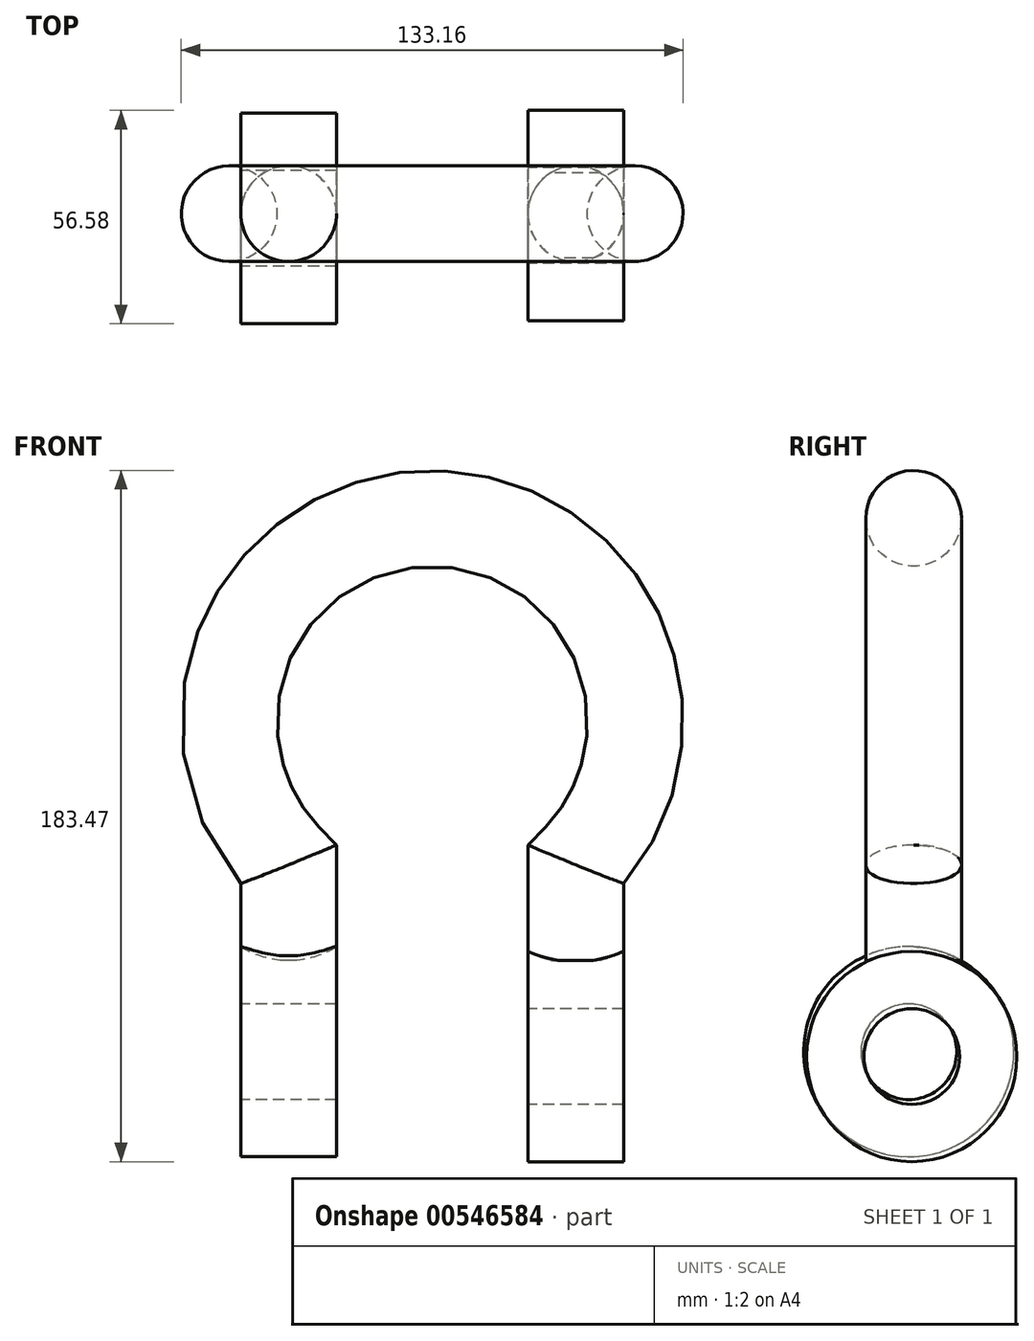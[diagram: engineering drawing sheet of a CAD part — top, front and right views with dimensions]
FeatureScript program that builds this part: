
annotation { "Feature Type Name" : "Feature", "Feature Type Description" : "" }
export const myFeature = defineFeature(function(context is Context, id is Id, definition is map)
    precondition{}
    {
        {
            var Q0;
            Q0=qCreatedBy(makeId("Top.planeOp"),FACE);
            var sketch = newSketch(context, id + "F0", { "sketchPlane" : qUnion([Q0])});
            skCircle(sketch, "E0", {"center": v(0, 0) * mm, "radius": 12.7 * mm});
            skSolve(sketch);
        }
        {
            var Q0;
            Q0=qCreatedBy(makeId("Front.planeOp"),FACE);
            var sketch = newSketch(context, id + "F1", { "sketchPlane" : qUnion([Q0])});
            skLineSegment(sketch, "E1", {"start": v(0, 0) * mm, "end": v(0, 25.4) * mm});
            skLineSegment(sketch, "E2", {"start": v(76.2, 0) * mm, "end": v(76.2, 25.4) * mm});
            skArc(sketch, "E3", {"start": v(76.2, 25.4) * mm, "mid": v(38.1, 117.38) * mm, "end": v(0, 25.4) * mm});
            skSolve(sketch);
        }
        {
            var Q0;
            Q0=makeQuery(id+"F0.imprint","IMPRINT",FACE,{"disambiguationData":[TD([[makeQuery(id+"F0.imprint","IMPRINT",EDGE,{"derivedFrom":sQuery(id+"F0.wireOp",EDGE,"E0")}),1.0]])]});
            var Q1;
            Q1=sQuery(id+"F1.wireOp",EDGE,"E3");
            var Q2;
            Q2=sQuery(id+"F1.wireOp",EDGE,"E1");
            var Q3;
            Q3=sQuery(id+"F1.wireOp",EDGE,"E2");
            sweep(context, id + "F2", {"profiles" : qUnion([Q0]), "path" : qUnion([Q1, Q2, Q3])});
        }
        {
            var Q0;
            Q0=qCreatedBy(makeId("Right.planeOp"),FACE);
            var sketch = newSketch(context, id + "F3", { "sketchPlane" : qUnion([Q0])});
            skLineSegment(sketch, "E4", {"start": v(12.7, 25.4) * mm, "end": v(12.7, 0) * mm});
            skLineSegment(sketch, "E5", {"start": v(-12.7, 1.3) * mm, "end": v(-12.7, 25.4) * mm});
            skArc(sketch, "E6", {"start": v(-12.7, 1.3) * mm, "mid": v(-2.7, -52.1) * mm, "end": v(12.7, 0) * mm});
            skCircle(sketch, "E7", {"center": v(-1.27, -24.2) * mm, "radius": 12.7 * mm});
            skLineSegment(sketch, "E8", {"start": v(0, 0) * mm, "end": v(-1.27, -24.2) * mm, "construction": true});
            skCircle(sketch, "E9", {"center": v(-1.27, -24.2) * mm, "radius": 27.9 * mm});
            skSolve(sketch);
        }
        {
            var Q0;
            Q0=makeQuery(id+"F3.imprint","IMPRINT",FACE,{"disambiguationData":[TD([[makeQuery(id+"F3.imprint","IMPRINT",EDGE,{"derivedFrom":sQuery(id+"F3.wireOp",EDGE,"E7")}),-1.0]])]});
            var Q1;
            Q1=makeQuery(id+"F2.opSweep","CAP_FACE",FACE,{"disambiguationData":[OSD([sQuery(id+"F0.wireOp",EDGE,"E0"),sQuery(id+"F1.wireOp",VERTEX,"E2.start")])],"isStart":false});
            extrude(context, id + "F4", {"entities" : qUnion([Q0]), "operationType" : NewBodyOperationType.ADD, "depth" : 12.7 * mm, "endBoundEntityFace" : qUnion([Q1]), "offsetDistance" : 25.4 * mm, "hasSecondDirection" : true, "secondDirectionOppositeDirection" : true, "secondDirectionDepth" : 12.7 * mm});
        }
        {
            var Q0;
            Q0=qCreatedBy(makeId("Right.planeOp"),FACE);
            cPlane(context, id + "F5", {"entities" : qUnion([Q0]), "cplaneType" : CPlaneType.OFFSET, "offset" : 76.2 * mm, "width" : 152.4 * mm, "height" : 152.4 * mm});
        }
        {
            var Q0;
            Q0=qCreatedBy(id+"F5.planeOp",FACE);
            var sketch = newSketch(context, id + "F6", { "sketchPlane" : qUnion([Q0])});
            skLineSegment(sketch, "E10", {"start": v(13.48, 24.1) * mm, "end": v(13.48, -1.3) * mm});
            skLineSegment(sketch, "E11", {"start": v(-11.92, 0) * mm, "end": v(-11.92, 24.1) * mm});
            skArc(sketch, "E12", {"start": v(-11.92, 0) * mm, "mid": v(-1.91, -53.4) * mm, "end": v(13.48, -1.3) * mm});
            skCircle(sketch, "E13", {"center": v(-0.49, -25.5) * mm, "radius": 12.7 * mm});
            skLineSegment(sketch, "E14", {"start": v(0.78, -1.3) * mm, "end": v(-0.49, -25.5) * mm, "construction": true});
            skCircle(sketch, "E15", {"center": v(-0.49, -25.5) * mm, "radius": 27.9 * mm});
            skSolve(sketch);
        }
        {
            var Q0;
            Q0=makeQuery(id+"F6.imprint","IMPRINT",FACE,{"disambiguationData":[TD([[makeQuery(id+"F6.imprint","IMPRINT",EDGE,{"derivedFrom":sQuery(id+"F6.wireOp",EDGE,"E13")}),-1.0]])]});
            extrude(context, id + "F7", {"entities" : qUnion([Q0]), "operationType" : NewBodyOperationType.ADD, "depth" : 12.7 * mm, "offsetDistance" : 25.4 * mm, "hasSecondDirection" : true, "secondDirectionOppositeDirection" : true, "secondDirectionDepth" : 12.7 * mm});
        }
    });
